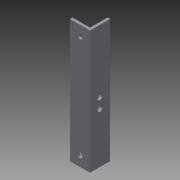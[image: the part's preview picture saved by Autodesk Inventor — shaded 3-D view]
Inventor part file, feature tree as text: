
AUTODESK INVENTOR PART (.ipt)
format: ipt  version: 2015 (Build 190159000, 159)  size: 97,792 bytes
history: native  units: in
note: dims shown in document units (in); Inventor stores cm internally (conversion verified against a paired STEP export)
features: sketch x3, hole x2, projected_geometry x2, extrude x1
ambient origin geometry x8: Origin, YZ Plane, XZ Plane, XY Plane, X Axis, Y Axis, Z Axis, Center Point
bodies: Solid1 (feature_tree)
feature tree (8):
  extrude  "Extrusion1"  Depth=0.125in
  hole  "Hole1"  [1 undecoded]
  hole  "Hole2"  [1 undecoded]
  sketch  "Sketch1"  dims[d0=1.0in d1=0.125in]
  sketch  "Sketch2"  dims[d2=0.125in d3=1.0in]
  projected_geometry  "Projected Loop1"
  sketch  "Sketch3"  dims[d4=6.125in d5=0.0in d6=0.5in d7=0.5in d8=2.5in d9=3.125in d10=0.25in d11=0.75in d12=0.375in d13=0.25in d14=0.5635in d15=1.0in d16=0.8108in d17=0.5in d18=0.5in d19=0.5in d20=0.5in d21=0.25in d22=0.75in d23=0.375in d24=0.25in d25=0.5635in d26=1.0in d27=0.8108in]
  projected_geometry  "Projected Loop2"
note: 2 required parameter values undecoded (feature->parameter linkage not recoverable at this tier; creation-order binding heuristic only, values carry confidence <= 0.55)
